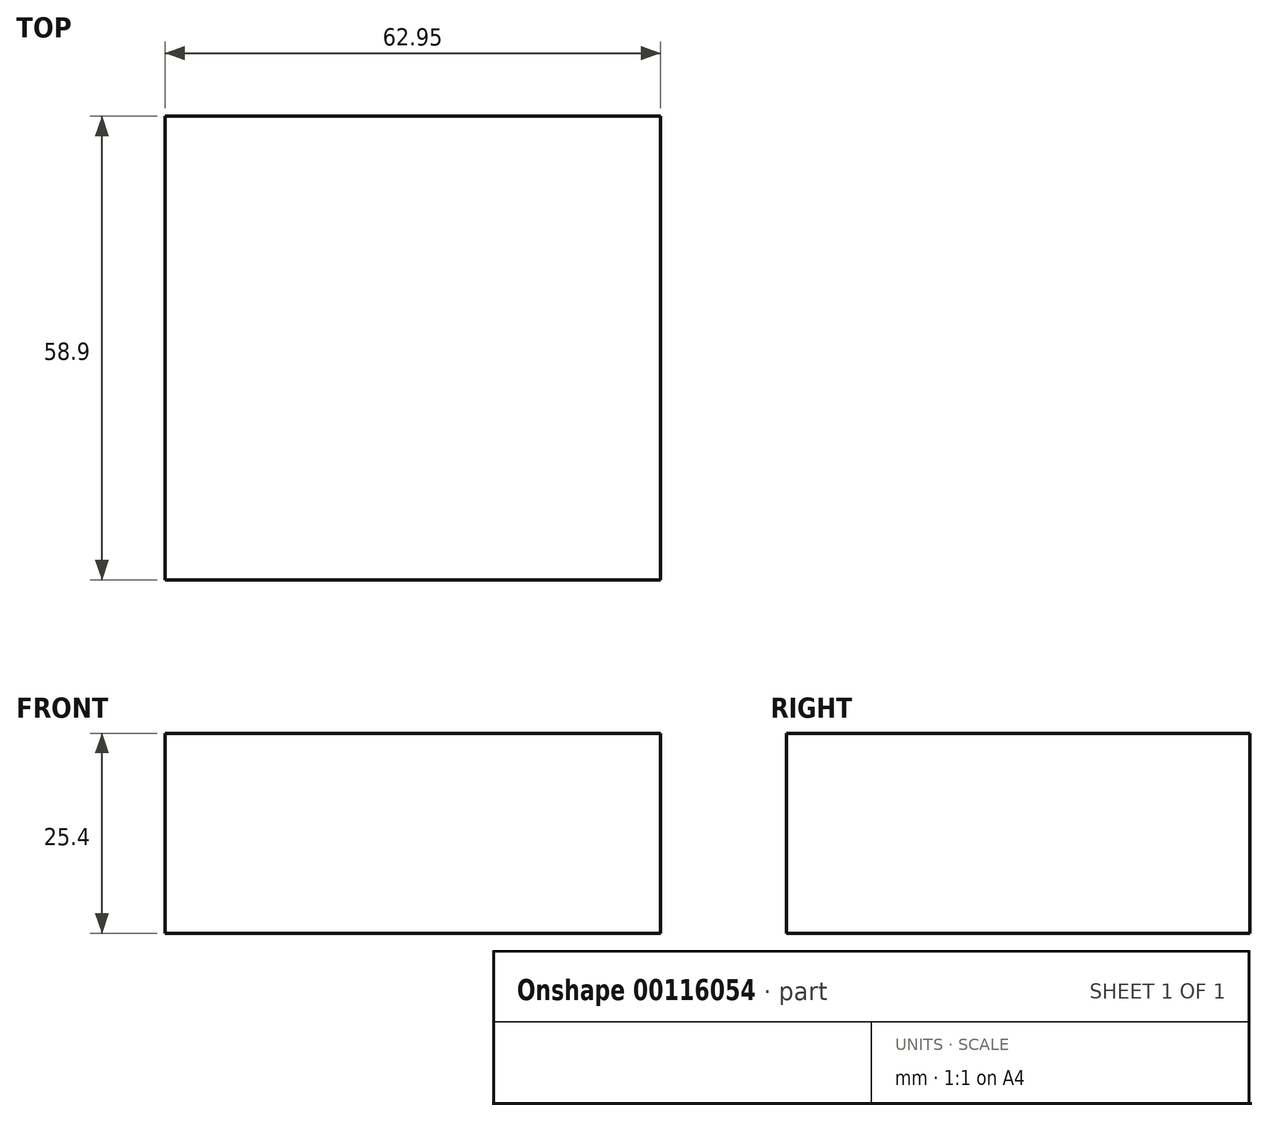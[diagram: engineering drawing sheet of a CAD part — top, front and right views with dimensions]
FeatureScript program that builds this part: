
annotation { "Feature Type Name" : "Feature", "Feature Type Description" : "" }
export const myFeature = defineFeature(function(context is Context, id is Id, definition is map)
    precondition{}
    {
        {
            var Q0;
            Q0=qCreatedBy(makeId("Top.planeOp"),FACE);
            var sketch = newSketch(context, id + "F0", { "sketchPlane" : qUnion([Q0])});
            skLineSegment(sketch, "E0.bottom", {"start": v(0, 0) * mm, "end": v(62.95, 0) * mm});
            skLineSegment(sketch, "E0.top", {"start": v(0, 58.9) * mm, "end": v(62.95, 58.9) * mm});
            skLineSegment(sketch, "E0.left", {"start": v(0, 0) * mm, "end": v(0, 58.9) * mm});
            skLineSegment(sketch, "E0.right", {"start": v(62.95, 0) * mm, "end": v(62.95, 58.9) * mm});
            skSolve(sketch);
        }
        {
            var Q0;
            Q0=makeQuery(id+"F0.imprint","IMPRINT",FACE,{"disambiguationData":[TD([[makeQuery(id+"F0.imprint","IMPRINT",EDGE,{"derivedFrom":sQuery(id+"F0.wireOp",EDGE,"E0.bottom")}),1.0]])]});
            extrude(context, id + "F1", {"entities" : qUnion([Q0]), "depth" : 25.4 * mm});
        }
    });
